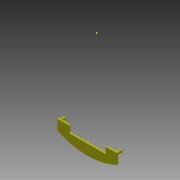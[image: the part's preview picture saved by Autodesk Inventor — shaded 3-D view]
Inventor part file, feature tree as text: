
AUTODESK INVENTOR PART (.ipt)
format: ipt  version: 2015 (Build 190159000, 159)  size: 474,624 bytes
history: native  units: mm
features: extrude x21, sketch x17, fillet x10, other x1, revolve x1
ambient origin geometry x8: Origin, YZ Plane, XZ Plane, XY Plane, X Axis, Y Axis, Z Axis, Center Point
bodies: Body1 (feature_tree)
feature tree (50):
  other  "Sólido1"
  sketch  "Boceto1"  dims[d0=37.0mm d1=57.0mm]
  extrude  "Extrusión1"  Depth=57.0mm
  extrude  "Extrusión2"  Depth=10.0mm
  extrude  "Extrusión3"  Depth=57.0mm
  sketch  "Boceto3"  dims[d4=20.0mm d5=57.0mm]
  extrude  "Extrusión4"  Depth=79.0mm
  extrude  "Extrusión5"  Depth=36.0mm
  extrude  "Extrusión6"  Depth=72.0mm
  extrude  "Extrusión7"  Depth=3.0mm
  fillet  "Empalme2"  Radius=3.0mm
  fillet  "Empalme3"  Radius=40.0mm
  fillet  "Empalme4"  Radius=13.0mm
  fillet  "Empalme5"  Radius=1111.0mm
  extrude  "Extrusión10"  Depth=5.0mm TaperAngle=0.0deg
  fillet  "Empalme10"  Radius=111.0mm
  sketch  "Boceto6"  dims[d6=37.0mm d7=79.0mm]
  extrude  "Extrusión11"  Depth=1.0mm
  extrude  "Extrusión12"  Depth=3.0mm
  fillet  "Empalme11"  Radius=2.0mm
  fillet  "Empalme12"  Radius=3.0mm
  revolve  "Revolución1"  [1 undecoded]
  fillet  "Empalme13"  Radius=6.5mm
  extrude  "Extrusión14"  Depth=3.0mm TaperAngle=0.0deg
  extrude  "Extrusión15"  Depth=1.0mm
  extrude  "Extrusión16"  Depth=19.5mm
  extrude  "Extrusión17"  Depth=10.0mm
  extrude  "Extrusión19"  Depth=10.0mm TaperAngle=0.0deg
  extrude  "Extrusión20"  Depth=8.0mm TaperAngle=0.0deg
  extrude  "Extrusión21"  Depth=10.0mm
  fillet  "Empalme14"  Radius=75.0mm
  extrude  "Extrusión22"  Depth=10.0mm
  extrude  "Extrusión23"  Depth=10.0mm
  fillet  "Empalme15"  Radius=20.0mm
  extrude  "Extrusión24"  Depth=10.0mm
  sketch  "Boceto20"  dims[d67=270.0mm d68=10.0mm d69=0.0mm]
  extrude  "Extrusión25"  Depth=10.0mm TaperAngle=0.0deg
  sketch  "Boceto2"  dims[d2=20.0mm d3=10.0mm]
  sketch  "Boceto8"  dims[d8=6.0mm d9=36.0mm]
  sketch  "Boceto9"  dims[d10=7.0mm d11=72.0mm]
  sketch  "Boceto10"  dims[d16=290.0mm d17=5.0mm d18=3.0mm d19=0.0mm d20=40.0mm d21=0.0mm d22=13.0mm d23=1111.0mm d24=0.0mm]
  sketch  "Boceto11"  dims[d25=5.0mm d26=0.0mm d27=5.0mm d28=0.0mm d29=111.0mm d30=0.0mm]
  sketch  "Boceto12"  dims[d31=3.0mm d32=0.0mm d41=1.0mm]
  sketch  "Boceto14"  dims[d42=5.0mm d43=5.0mm d44=2.0mm d47=3.0mm d48=0.0mm]
  sketch  "Boceto15"  dims[d51=1.0mm d53=2.5mm d54=6.5mm]
  sketch  "Boceto16"  dims[d55=3.0mm d56=0.0mm d57=3.0mm d58=0.0mm]
  sketch  "Boceto17"  dims[d59=1.0mm d60=2.0mm]
  sketch  "Boceto18"  dims[d63=19.5mm d64=19.5mm]
  sketch  "Boceto19"  dims[d65=180.0deg d66=10.0mm]
  sketch  "Boceto21"  dims[d70=292.0mm d71=300.0mm d72=270.0mm d73=10.0mm d74=6.0mm d75=3.0mm d76=0.5mm d77=35.0mm d78=3.0mm d79=0.5mm d80=6.0mm d81=35.0mm d82=40.0mm d84=360.0deg d86=8.0mm d87=0.0mm d88=20.0mm d89=75.0mm d90=40.0mm d91=140.0mm d92=20.0mm d93=20.0mm d94=111.0mm d95=0.0mm d96=5.0mm d97=70.0mm d98=5.0mm d99=70.0mm d100=5.0mm d101=10.0mm d102=0.0mm d110=3.0mm d111=3.0mm d112=3.0mm d113=3.0mm d114=10.0mm d115=0.0mm d116=0.3mm d117=10.0mm d118=0.0mm d119=8.0mm d120=16.0mm d121=10.0mm d122=0.0mm d123=4.0mm d124=4.2mm d125=111.0mm d126=0.0mm d127=8.0mm d128=16.0mm d129=10.0mm d130=0.0mm d131=4.0mm d132=4.2mm d133=111.0mm d134=0.0mm d135=111.0mm d136=0.0mm]
note: 1 required parameter value undecoded (feature->parameter linkage not recoverable at this tier; creation-order binding heuristic only, values carry confidence <= 0.55)
